# Revit family: QF_Stero_SC-24-ELECTRIC_(L-R)
name_source: partatom
category: Specialty Equipment
revit_build: Autodesk Revit 2017 (Build: 20190508_0315(x64)
units: mm (PartAtom-declared; Revit-internal decimal feet)

## family parameters
Always vertical = Yes
Cut with Voids When Loaded = No
OmniClass Number = 23.40.40.14.31
OmniClass Title = Cleaning and Disposal Equipment
Part Type = Normal
Room Calculation Point = No
Round Connector Dimension = Use Diameter
Shared = No
Work Plane-Based = No

## types (6) — shared parameters
Accent Material = QF_Plastic-Black
Apparent Power = 13 kW
Assembly Code = E1090320
Booster Apparent Power = 0 kW
Booster Con Conduit = Yes
Booster Cycle = 60 Hz
Booster Elec Conn Connection Height = 6"
Booster Elec Conn RI Height = 0"
Booster Electrical Connection Type = HARDWIRE
Booster Number of Poles  = 3
Booster Phase = 3
CSI MasterFormat = 11 48 13
Clearance Material = QF_Finishes_Clearances
Cold Water Connection Height = 60"
Cold Water Maximum Pressure = 40.00 psi
Cold Water Minimum Pressure = 20.00 psi
Cold Water Size = 1"
Curtain Material = QF_Plastic-Cyan
Cycle = 60 Hz
Depth = 40"
Description = DISHWASHING MACHINE WITH BOOSTER
Elec Conn Connection Height = 68 1/2"
Elec Conn RI Height = 0"
Exhaust Vent Depth = 24 7/8"
Exhaust Vent Width = 3 7/8"
Exhaust Volume-Load End = 200 CFM
Exhaust Volume-Unload End = 400 CFM
Foodservice Equipment Identifier = Yes
HP = 2
Handle Material = QF_Plastic-Blue
Height = 71 1/2"
Hot Water Connection Height = 60"
Hot Water Consumption = 5 GPM
Hot Water Flow = 0 GPM
Hot Water Maximum Pressure = 20.00 psi
Hot Water Minimum Pressure = 20.00 psi
Hot Water Size = 1"
Indirect Waste Connection Height = 8 1/2"
Indirect Waste Size = 2"
Manufacturer = STERO
Material = QF_Metal-Stainless-Satin
Model = SC-24 ELECTRIC WITH BOOSTER
Number of Poles = 3
Phase = 3
URL = WWW.STERO.COM
Width = 88"

## per-type parameters (varying)
| type | Booster FL Amps | Booster Max Overcurrent Protection | Booster Volts | FL Amps | Hot Water Temperature | Max Overcurrent Protection | Volts |
| 208/60/3-36KW_BOOSTER | 100 A | 125 A | 208 V | 35 A | 140 °F | 50 A | 208 V |
| 240/60/3-36KW_BOOSTER | 87 A | 125 A | 240 V | 34 A | 140 °F | 50 A | 240 V |
| 480/60/3-36KW_BOOSTER | 43 A | 60 A | 480 V | 16 A | 140 °F | 20 A | 480 V |
| 208/60/3-57KW_BOOSTER | 158 A | 200 A | 208 V | 35 A | 110 °F | 50 A | 208 V |
| 240/60/3-57KW_BOOSTER | 137 A | 175 A | 240 V | 34 A | 110 °F | 50 A | 240 V |
| 480/60/3-57KW_BOOSTER | 69 A | 90 A | 480 V | 16 A | 110 °F | 20 A | 480 V |

## geometry (parser evidence)
native form markers: Sweep x5
no freeform markers — native parametric forms only
